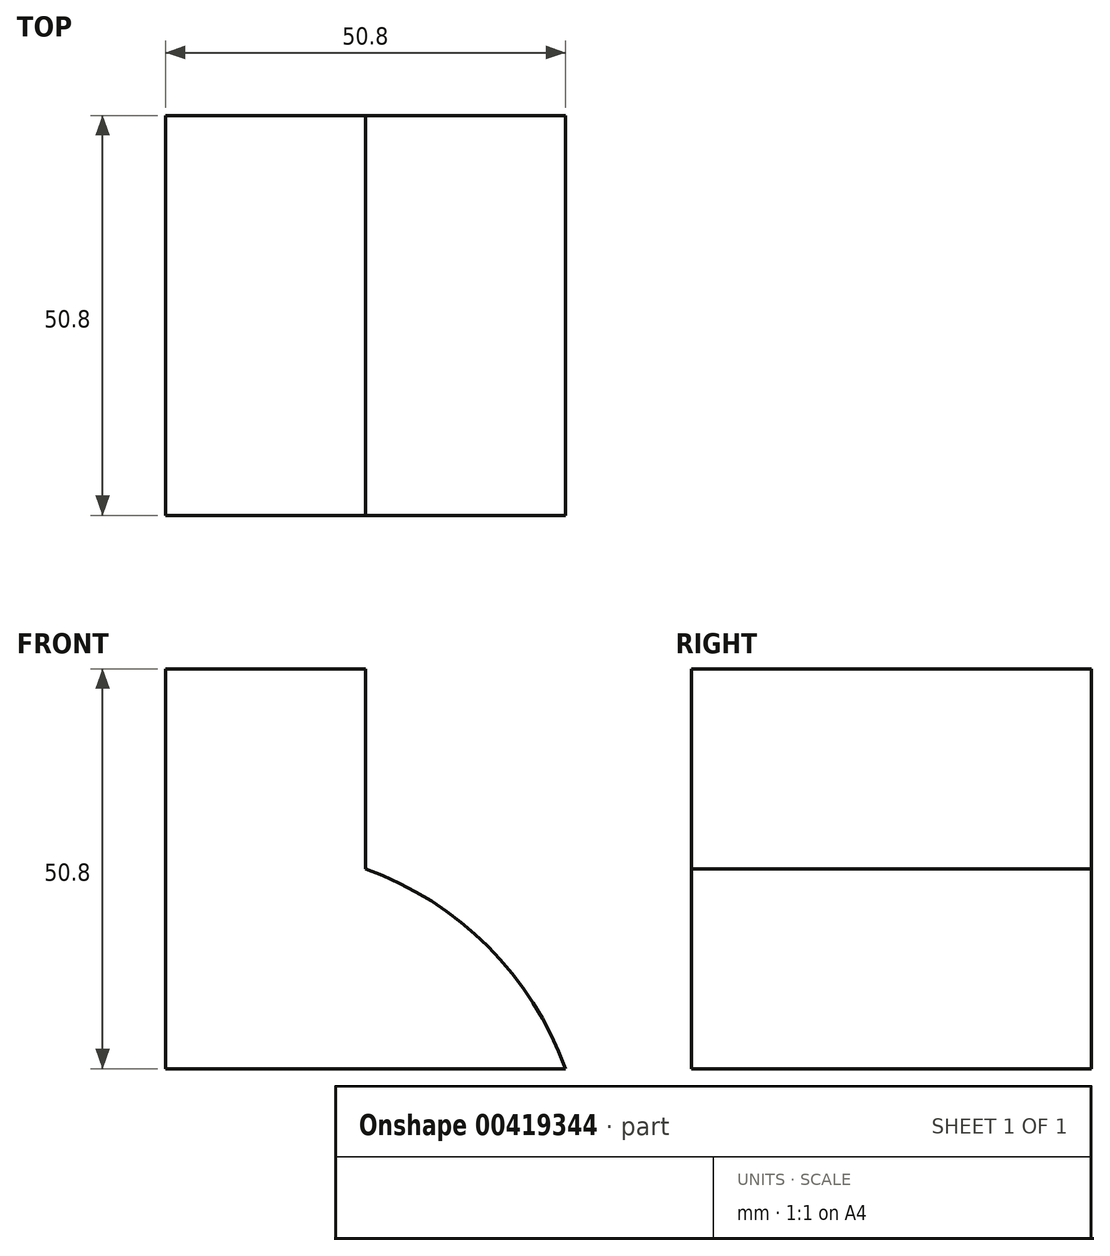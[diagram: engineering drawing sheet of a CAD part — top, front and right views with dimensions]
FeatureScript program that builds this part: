
annotation { "Feature Type Name" : "Feature", "Feature Type Description" : "" }
export const myFeature = defineFeature(function(context is Context, id is Id, definition is map)
    precondition{}
    {
        {
            var Q0;
            Q0=qCreatedBy(makeId("Front.planeOp"),FACE);
            var sketch = newSketch(context, id + "F0", { "sketchPlane" : qUnion([Q0])});
            skLineSegment(sketch, "E0", {"start": v(0, 0) * mm, "end": v(-50.8, 0) * mm});
            skLineSegment(sketch, "E1", {"start": v(-50.8, 0) * mm, "end": v(-50.8, 50.8) * mm});
            skLineSegment(sketch, "E2", {"start": v(-50.8, 50.8) * mm, "end": v(-25.4, 50.8) * mm});
            skLineSegment(sketch, "E3", {"start": v(-25.4, 50.8) * mm, "end": v(-25.4, 25.4) * mm});
            skArc(sketch, "E4", {"start": v(0, 0) * mm, "mid": v(-9.88, 15.52) * mm, "end": v(-25.4, 25.4) * mm});
            skSolve(sketch);
        }
        {
            var Q0;
            Q0 = qSketchRegion(id + "F0", true);
            extrude(context, id + "F1", {"entities" : qUnion([Q0]), "depth" : 50.8 * mm});
        }
    });
